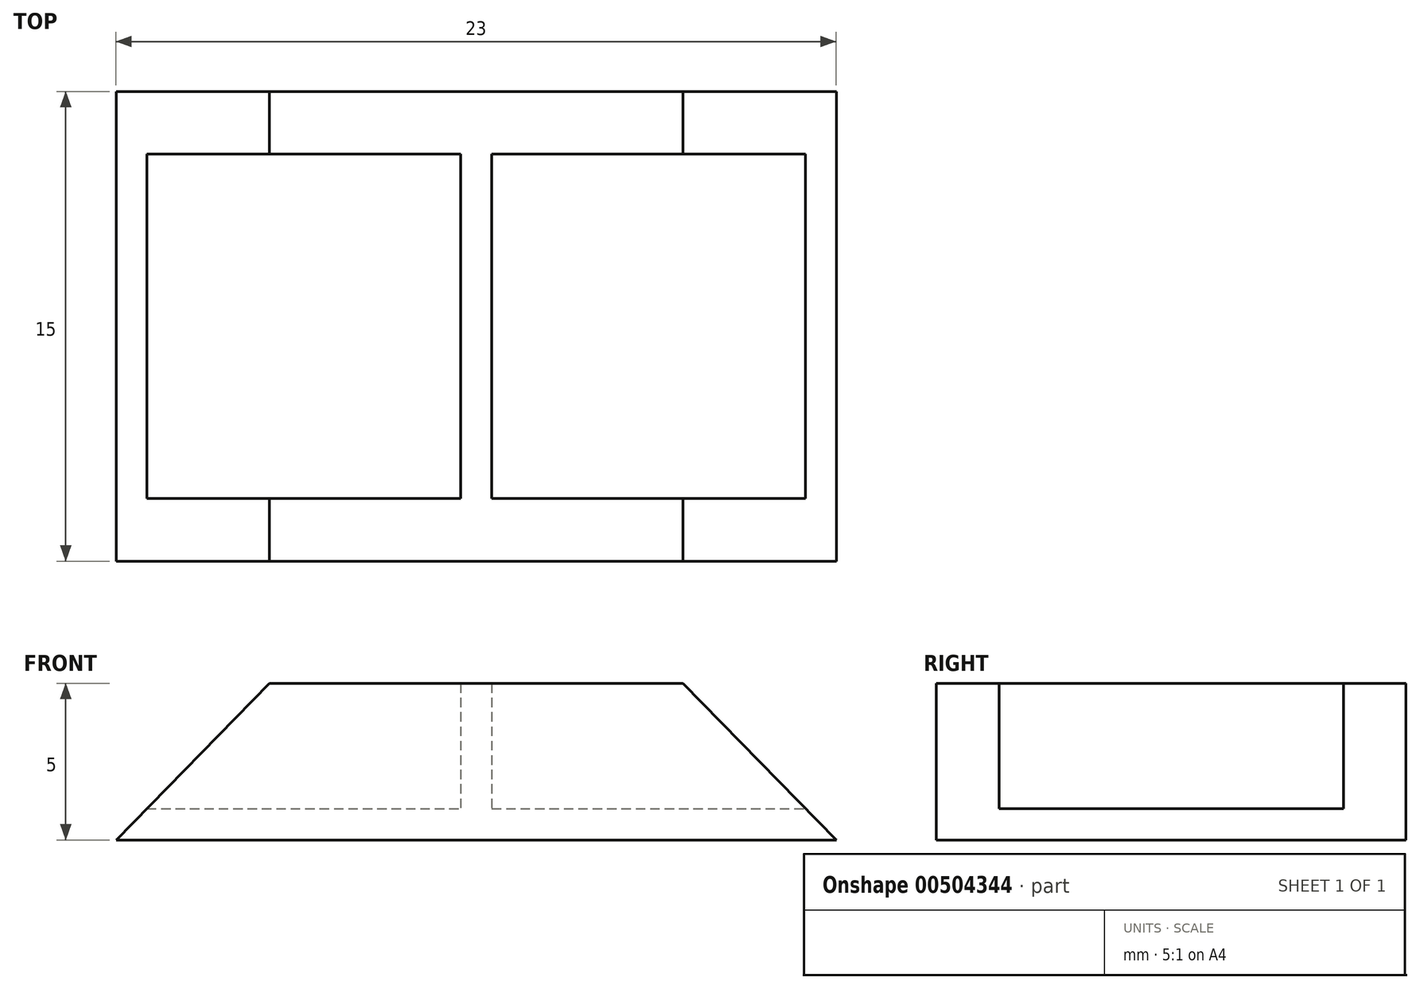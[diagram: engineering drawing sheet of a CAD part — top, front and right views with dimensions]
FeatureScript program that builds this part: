
annotation { "Feature Type Name" : "Feature", "Feature Type Description" : "" }
export const myFeature = defineFeature(function(context is Context, id is Id, definition is map)
    precondition{}
    {
        {
            var Q0;
            Q0=qCreatedBy(makeId("Front.planeOp"),FACE);
            var sketch = newSketch(context, id + "F0", { "sketchPlane" : qUnion([Q0])});
            skLineSegment(sketch, "E0", {"start": v(-11.46, 0) * mm, "end": v(11.54, 0) * mm});
            skLineSegment(sketch, "E1", {"start": v(11.54, 0) * mm, "end": v(6.64, 5) * mm});
            skLineSegment(sketch, "E2", {"start": v(6.64, 5) * mm, "end": v(-6.56, 5) * mm});
            skLineSegment(sketch, "E3", {"start": v(-6.56, 5) * mm, "end": v(-11.46, 0) * mm});
            skSolve(sketch);
        }
        {
            var Q0;
            Q0=makeQuery(id+"F0.imprint","IMPRINT",FACE,{"disambiguationData":[TD([[makeQuery(id+"F0.imprint","IMPRINT",EDGE,{"derivedFrom":sQuery(id+"F0.wireOp",EDGE,"E0")}),1.0]])]});
            extrude(context, id + "F1", {"entities" : qUnion([Q0]), "depth" : 15 * mm});
        }
        {
            var Q0;
            Q0=makeQuery(id+"F1.opExtrude","SWEPT_FACE",FACE,{"disambiguationData":[OSD([sQuery(id+"F0.wireOp",EDGE,"E2")])]});
            var sketch = newSketch(context, id + "F2", { "sketchPlane" : qUnion([Q0])});
            skLineSegment(sketch, "E4.bottom", {"start": v(-11.46, -13) * mm, "end": v(11.54, -13) * mm});
            skLineSegment(sketch, "E4.top", {"start": v(-11.46, -2) * mm, "end": v(11.54, -2) * mm});
            skLineSegment(sketch, "E4.left", {"start": v(-11.46, -13) * mm, "end": v(-11.46, -2) * mm});
            skLineSegment(sketch, "E4.right", {"start": v(11.54, -13) * mm, "end": v(11.54, -2) * mm});
            skSolve(sketch);
        }
        {
            var Q0;
            Q0 = qSketchRegion(id + "F2", true);
            extrude(context, id + "F3", {"entities" : qUnion([Q0]), "operationType" : NewBodyOperationType.REMOVE, "oppositeDirection" : true, "depth" : 4 * mm});
        }
        {
            var Q0;
            Q0=makeQuery(id+"F3.boolean.opBoolean","COPY",FACE,{"derivedFrom":makeQuery(id+"F3.opExtrude","CAP_FACE",FACE,{"disambiguationData":[OSD([sQuery(id+"F2.wireOp",EDGE,"E4.bottom"),sQuery(id+"F2.wireOp",EDGE,"E4.top"),sQuery(id+"F2.wireOp",EDGE,"E4.left"),sQuery(id+"F2.wireOp",EDGE,"E4.right")])],"isStart":false})});
            var sketch = newSketch(context, id + "F4", { "sketchPlane" : qUnion([Q0])});
            skLineSegment(sketch, "E5.bottom", {"start": v(-0.46, -2) * mm, "end": v(0.54, -2) * mm});
            skLineSegment(sketch, "E5.top", {"start": v(-0.46, -13) * mm, "end": v(0.54, -13) * mm});
            skLineSegment(sketch, "E5.left", {"start": v(-0.46, -2) * mm, "end": v(-0.46, -13) * mm});
            skLineSegment(sketch, "E5.right", {"start": v(0.54, -2) * mm, "end": v(0.54, -13) * mm});
            skSolve(sketch);
        }
        {
            var Q0;
            Q0=makeQuery(id+"F4.imprint","IMPRINT",FACE,{"disambiguationData":[TD([[makeQuery(id+"F4.imprint","IMPRINT",EDGE,{"derivedFrom":sQuery(id+"F4.wireOp",EDGE,"E5.bottom")}),-1.0]])]});
            extrude(context, id + "F5", {"entities" : qUnion([Q0]), "operationType" : NewBodyOperationType.ADD, "depth" : 4 * mm});
        }
    });
